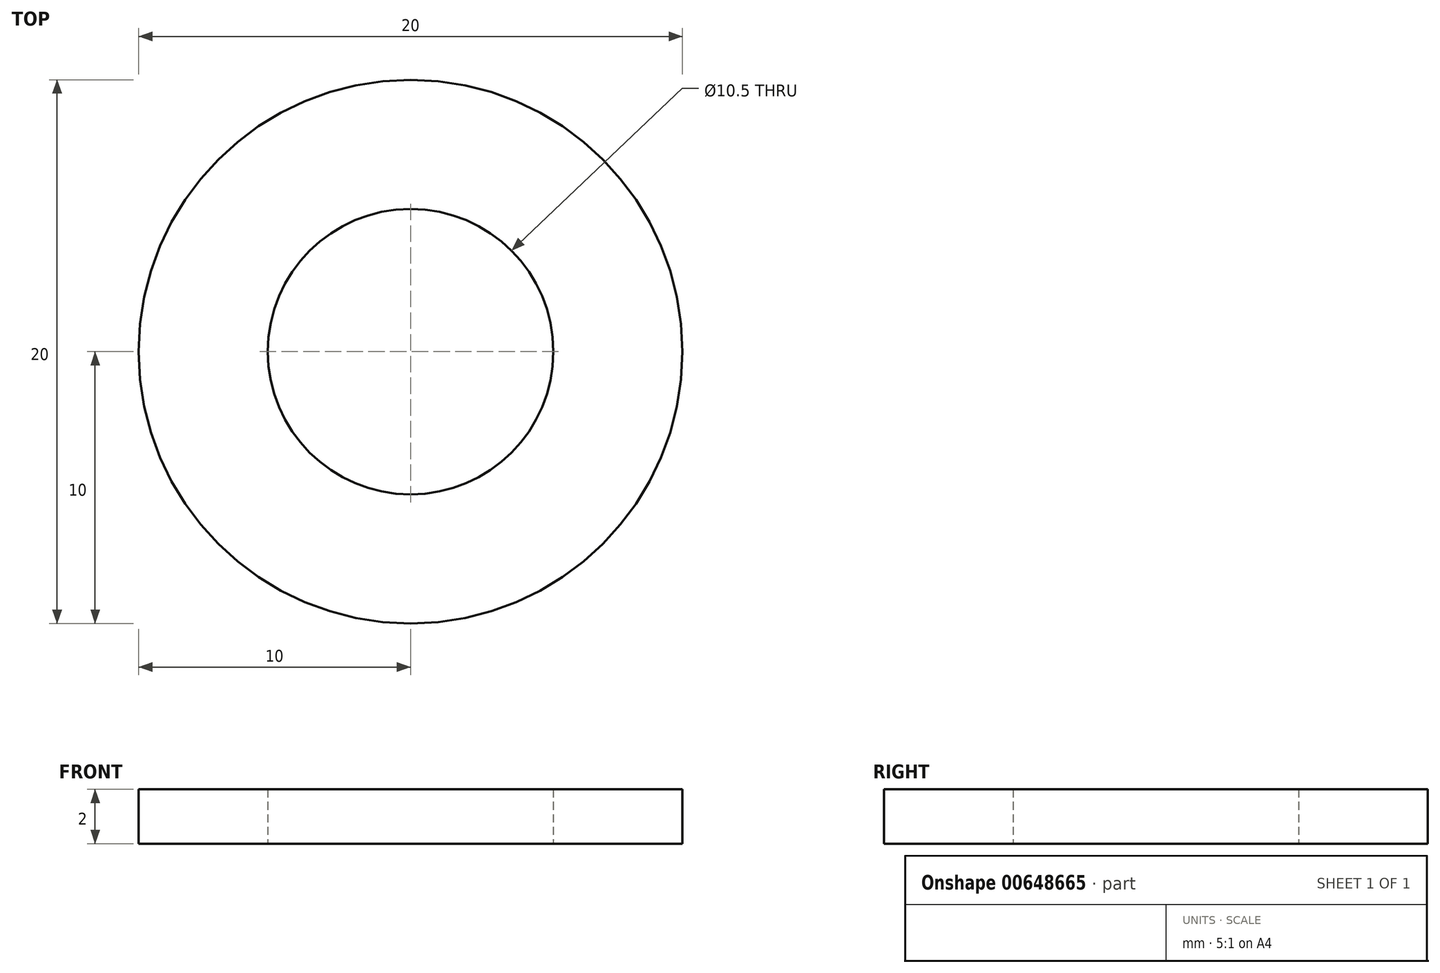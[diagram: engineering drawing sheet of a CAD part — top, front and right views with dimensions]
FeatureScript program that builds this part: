
annotation { "Feature Type Name" : "Feature", "Feature Type Description" : "" }
export const myFeature = defineFeature(function(context is Context, id is Id, definition is map)
    precondition{}
    {
        {
            var Q0;
            Q0=qCreatedBy(makeId("Top.planeOp"),FACE);
            var sketch = newSketch(context, id + "F0", { "sketchPlane" : qUnion([Q0])});
            skCircle(sketch, "E0", {"center": v(0, 0) * mm, "radius": 10 * mm});
            skCircle(sketch, "E1", {"center": v(0, 0) * mm, "radius": 5.25 * mm});
            skSolve(sketch);
        }
        {
            var Q0;
            Q0=makeQuery(id+"F0.imprint","IMPRINT",FACE,{"disambiguationData":[TD([[makeQuery(id+"F0.imprint","IMPRINT",EDGE,{"derivedFrom":sQuery(id+"F0.wireOp",EDGE,"E0")}),1.0]])]});
            extrude(context, id + "F1", {"entities" : qUnion([Q0]), "depth" : 2 * mm, "offsetDistance" : 25 * mm});
        }
    });
